# Revit family: Sirena algoritmica_Aguilera Electronica
name_source: partatom
category: Dispositivos de alarma de incendios
units: mm (PartAtom-declared; Revit-internal decimal feet)

## family parameters
Anfitrión = Cara
Compartido = No
Corte con vacíos al cargar = No
Cota de conector redondo = Diámetro de uso
Mantener orientación de anotación = Sí
Número OmniClass = 23.85.30.21.14.11
Punto de cálculo de habitación = No
Tipo de pieza = Normal
Título OmniClass = Concentration Detection Bells and Sounders

## types (4) — shared parameters
Altura 1 = 10 mm  [stored 0.0328084 ft]
Altura 2 = 53 mm  [stored 0.173885 ft]
Altura 3 = 17 mm
Diámetro tubo = 20 mm  [stored 0.0656168 ft]
Fabricante = Aguilera Electrónica
Símbolo = Sí
Símbolo texto modelo = Sí
zero-valued in all types: Elevación por defecto

## per-type parameters (varying)
| type | Descripción | Foco | IP66 | Interior | Modelo | Sirena | URL |
| Sirena algorítmica | Sirena de bajo consumo multitono. Certificada según EN 54-3. Consumo entre 6 y 33 mA, dependiendo del tono. Nivel sonoro: 102 dB (tono 3).
Dimensiones: Ø 93 mm, altura: 63mm. Incluye base alta.
Incorpora un módulo microprocesado para su integración directa en el bucle algorítmico. | No | No | No | AE/SA-AS1 | Sí | http://aguilera.es |
| Sirena bucle algorítmico con aislador | Sirena de bajo consumo multitono. Certificada según EN 54-3. Consumo entre 6 y 33 mA, dependiendo del tono. Nivel sonoro: 102 dB (tono 3). Incorpora un módulo microprocesado para su integración directa en el bucle algorítmico.
Dimensiones: Ø 93 mm, altura: 63mm. Incluye base alta. | No | No | No | AE/SA-AS1A | Sí | http://aguilera.es |
| Sirena con foco con aislador bucle algorítmico | Sirena acústica con foco de bajo consumo para uso interior certificada EN54:3 y EN54:23, con módulo de control y circuito aislador bidireccional integrado certificado EN54:17 y EN54-18, diseñada para ser utilizada con las centrales de detección de incendio algorítmicas de AGUILERA ELECTRONICA.

La sirena puede configurarse como elemento óptico-acústico (flash + sonido) o solo óptico (flash). Pueden configurarse 2 niveles de sonido según necesidad.

El conexionado de la instalación debe realizarse cumpliendo con los requerimientos de la normativa UNE 23007-14:2014. En caso de cortocircuito en el cableado de uno de los extremos del bucle algorítmico, la sirena siempre permanecerá operativa.

El circuito aislador bidireccional permite aislar cortocircuitos en el cableado del bucle de detección algorítmico, dejando fuera de servicio la zona afectada entre 2 aisladores para instalaciones realizadas en bucle cerrado.

El circuito aislador incorpora las siguientes funciones:

• Interruptor bidireccional, permite cortar el bucle de forma segura, sin provocar caídas de tensión cuando da continuidad.
• Detector de tensión. Supervisa la tensión del bucle, impidiendo su funcionamiento hasta que la tensión no supera el límite inferior fijado.
• Indicador luminoso, se activa cuando se detecta un corto en el bucle, o un consumo de corriente excesivo.

La sirena es personalizada en la Central Algorítmica con el nombre de la zona donde se encuentra instalada. Cada sirena incorpora un módulo que la identifica individualmente con un número dentro del bucle de la instalación. Este número se almacena en memoria EEPROM por lo que se mantiene aunque la sirena esté sin alimentación durante un largo tiempo.

La sirena AE/SA-ASF23 se alimenta desde el propio bucle algorítmico. El número máximo de sirenas que pueden ser conectadas en el mismo lazo depende del número de equipos conectados y el consumo presente en el bucle. | Sí | No | Sí | AE/SA-ASF23 | No | https://aguilera.es |
| Sirena con foco con aislador bucle algorítmico exterior | Sirena acústica con foco de bajo consumo para uso exterior certificada EN 54-3 y EN 54-23.
Grado de protección IP66, y módulo de control y circuito aislador bidireccional integrado certificado EN54:17 y EN54-18, diseñada para su integración en los bucles de detección de incendio algorítmicos
de AGUILERA ELECTRONICA. La sirena AE/SA-ASF23 se alimenta desde el propio bucle algorítmico.
Dimensiones Ancho 110mm, Altura 100 mm. Intensidad sonora 99±3 dB(A). Clase WO. | Sí | Sí | No | AE/SA-ASF23WP | Sí | https://aguilera.es |

note: [stored X ft] marks values corroborated as IEEE doubles in the binary element streams (Revit-internal decimal feet)
